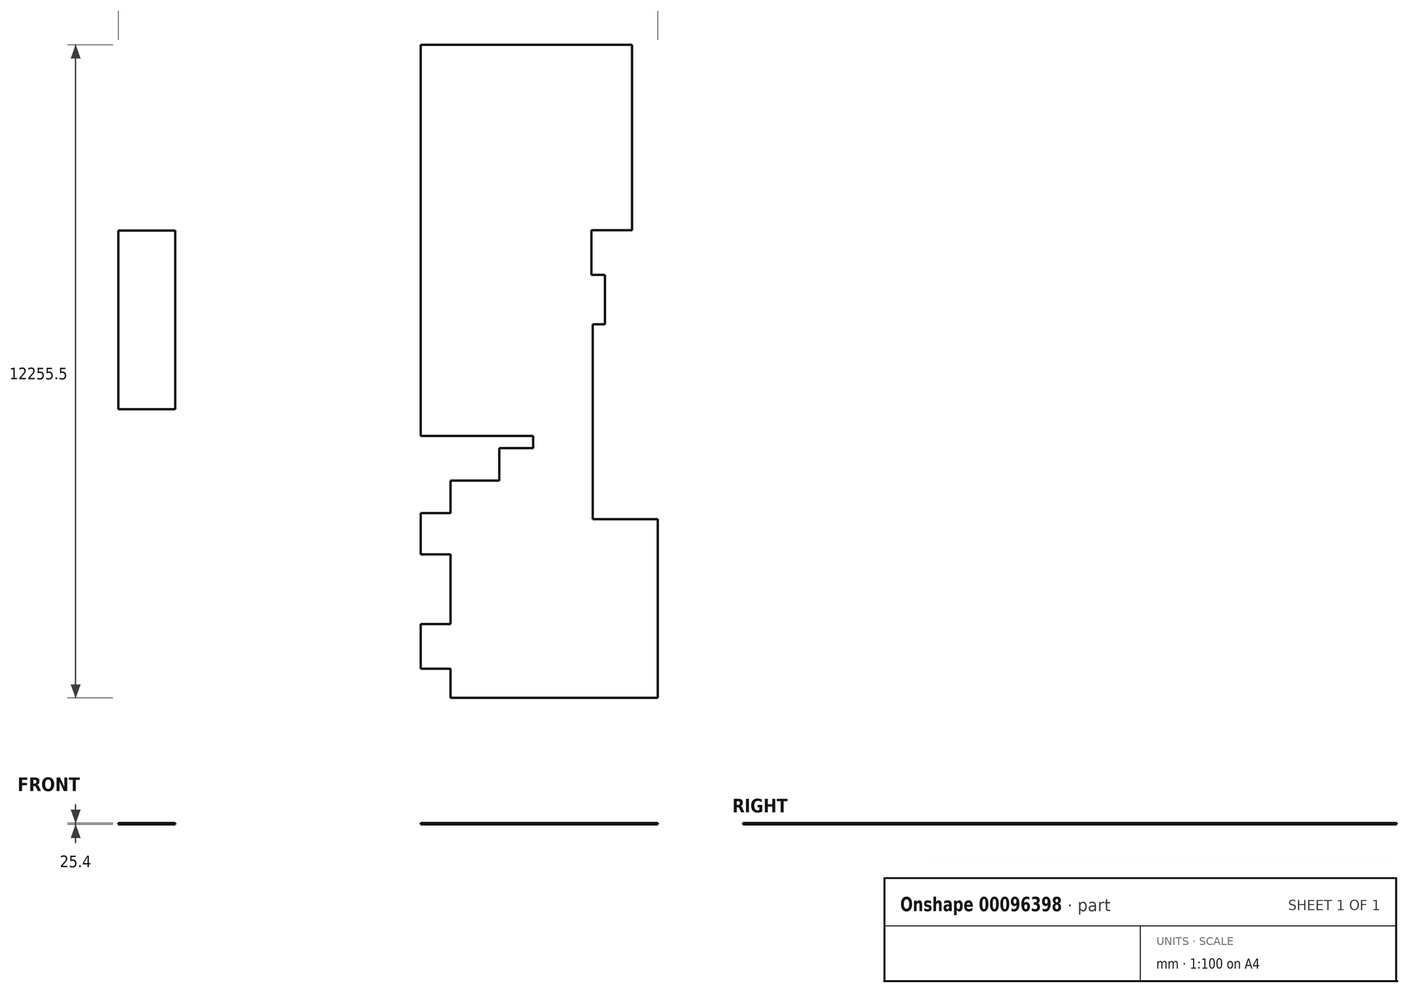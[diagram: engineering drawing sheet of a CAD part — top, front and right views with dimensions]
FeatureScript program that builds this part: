
annotation { "Feature Type Name" : "Feature", "Feature Type Description" : "" }
export const myFeature = defineFeature(function(context is Context, id is Id, definition is map)
    precondition{}
    {
        {
            var Q0;
            Q0=qCreatedBy(makeId("Top.planeOp"),FACE);
            var sketch = newSketch(context, id + "F0", { "sketchPlane" : qUnion([Q0])});
            skLineSegment(sketch, "E0", {"start": v(0, 0) * mm, "end": v(3962.4, 0) * mm});
            skLineSegment(sketch, "E1", {"start": v(0, 0) * mm, "end": v(0, -7340.6) * mm});
            skLineSegment(sketch, "E2", {"start": v(3962.4, 0) * mm, "end": v(3962.4, -3479.8) * mm});
            skLineSegment(sketch, "E3", {"start": v(3962.4, -3479.8) * mm, "end": v(3200.4, -3479.8) * mm});
            skLineSegment(sketch, "E4", {"start": v(3200.4, -3479.8) * mm, "end": v(3200.4, -4318) * mm});
            skLineSegment(sketch, "E5", {"start": v(3200.4, -4318) * mm, "end": v(3454.4, -4318) * mm});
            skLineSegment(sketch, "E6", {"start": v(3454.4, -4318) * mm, "end": v(3454.4, -5245.1) * mm});
            skLineSegment(sketch, "E7", {"start": v(3454.4, -5245.1) * mm, "end": v(3225.8, -5245.1) * mm});
            skLineSegment(sketch, "E8", {"start": v(3225.8, -5245.1) * mm, "end": v(3225.8, -8902.7) * mm});
            skLineSegment(sketch, "E9", {"start": v(3225.8, -8902.7) * mm, "end": v(4445, -8902.7) * mm});
            skLineSegment(sketch, "E10", {"start": v(4445, -8902.7) * mm, "end": v(4445, -12255.5) * mm});
            skLineSegment(sketch, "E11", {"start": v(4445, -12255.5) * mm, "end": v(558.8, -12255.5) * mm});
            skLineSegment(sketch, "E12", {"start": v(0, -7340.6) * mm, "end": v(2108.2, -7340.6) * mm});
            skLineSegment(sketch, "E13", {"start": v(2108.2, -7340.6) * mm, "end": v(2108.2, -7569.2) * mm});
            skLineSegment(sketch, "E14", {"start": v(2108.2, -7569.2) * mm, "end": v(1473.2, -7569.2) * mm});
            skLineSegment(sketch, "E15", {"start": v(1473.2, -7569.2) * mm, "end": v(1473.2, -8178.8) * mm});
            skLineSegment(sketch, "E16", {"start": v(1473.2, -8178.8) * mm, "end": v(558.8, -8178.8) * mm});
            skLineSegment(sketch, "E17", {"start": v(558.8, -8178.8) * mm, "end": v(558.8, -8788.4) * mm});
            skLineSegment(sketch, "E18", {"start": v(558.8, -8788.4) * mm, "end": v(0, -8788.4) * mm});
            skLineSegment(sketch, "E19", {"start": v(0, -8788.4) * mm, "end": v(0, -9563.1) * mm});
            skLineSegment(sketch, "E20", {"start": v(0, -9563.1) * mm, "end": v(558.8, -9563.1) * mm});
            skLineSegment(sketch, "E21", {"start": v(558.8, -9563.1) * mm, "end": v(558.8, -10871.2) * mm});
            skPoint(sketch, "E21.endSnap0", {"position": v(558.8, -8483.6) * mm});
            skLineSegment(sketch, "E22", {"start": v(558.8, -10871.2) * mm, "end": v(0, -10871.2) * mm});
            skLineSegment(sketch, "E23", {"start": v(0, -10871.2) * mm, "end": v(0, -11709.4) * mm});
            skLineSegment(sketch, "E24", {"start": v(0, -11709.4) * mm, "end": v(558.8, -11709.4) * mm});
            skLineSegment(sketch, "E25", {"start": v(558.8, -11709.4) * mm, "end": v(558.8, -12255.5) * mm});
            skLineSegment(sketch, "E26.bottom", {"start": v(-5672.23, -3483.32) * mm, "end": v(-4605.43, -3483.32) * mm});
            skLineSegment(sketch, "E26.top", {"start": v(-5672.23, -6836.12) * mm, "end": v(-4605.43, -6836.12) * mm});
            skLineSegment(sketch, "E26.left", {"start": v(-5672.23, -3483.32) * mm, "end": v(-5672.23, -6836.12) * mm});
            skLineSegment(sketch, "E26.right", {"start": v(-4605.43, -3483.32) * mm, "end": v(-4605.43, -6836.12) * mm});
            skSolve(sketch);
        }
        {
            var Q0;
            Q0 = qSketchRegion(id + "F0", true);
            extrude(context, id + "F1", {"entities" : qUnion([Q0]), "depth" : 25.4 * mm});
        }
    });
